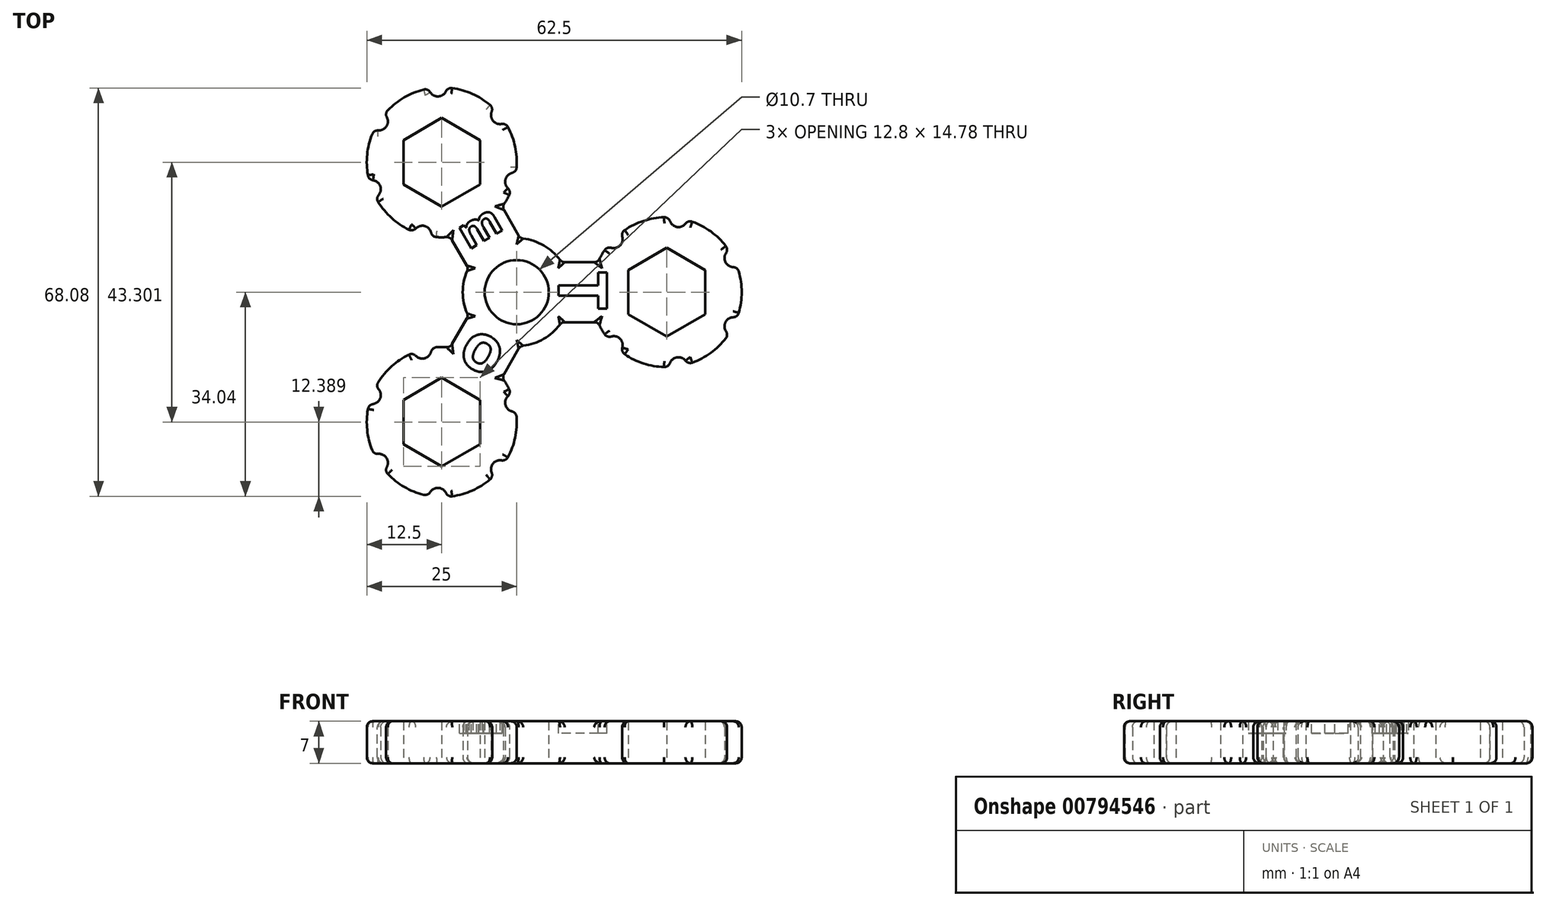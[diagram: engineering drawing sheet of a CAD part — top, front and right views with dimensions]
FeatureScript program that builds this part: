
annotation { "Feature Type Name" : "Feature", "Feature Type Description" : "" }
export const myFeature = defineFeature(function(context is Context, id is Id, definition is map)
    precondition{}
    {
        {
            var Q0;
            Q0=qCreatedBy(makeId("Top.planeOp"),FACE);
            var sketch = newSketch(context, id + "F0", { "sketchPlane" : qUnion([Q0])});
            skCircle(sketch, "E0", {"center": v(0, 0) * mm, "radius": 5.35 * mm});
            skCircle(sketch, "E1", {"center": v(0, 0) * mm, "radius": 9 * mm});
            skCircle(sketch, "E2", {"center": v(25, 0) * mm, "radius": 12.5 * mm});
            skLineSegment(sketch, "E3", {"start": v(7.48, 5) * mm, "end": v(19.48, 5) * mm});
            skLineSegment(sketch, "E4", {"start": v(7.48, -5) * mm, "end": v(19.48, -5) * mm});
            skCircle(sketch, "E5.cCircle", {"center": v(25, 0) * mm, "radius": 6.4 * mm, "construction": true});
            skLineSegment(sketch, "E5.0", {"start": v(31.4, 3.7) * mm, "end": v(31.4, -3.7) * mm});
            skLineSegment(sketch, "E5.1", {"start": v(31.4, -3.7) * mm, "end": v(25, -7.4) * mm});
            skLineSegment(sketch, "E5.2", {"start": v(25, -7.4) * mm, "end": v(18.6, -3.7) * mm});
            skLineSegment(sketch, "E5.3", {"start": v(18.6, -3.7) * mm, "end": v(18.6, 3.7) * mm});
            skLineSegment(sketch, "E5.4", {"start": v(18.6, 3.7) * mm, "end": v(25, 7.4) * mm});
            skLineSegment(sketch, "E5.5", {"start": v(25, 7.4) * mm, "end": v(31.4, 3.7) * mm});
            skPoint(sketch, "E5.0.midPoint", {"position": v(31.4, 0) * mm});
            skCircle(sketch, "E6.1.0", {"center": v(-12.5, 21.65) * mm, "radius": 12.5 * mm});
            skLineSegment(sketch, "E6.1.1", {"start": v(-18.9, 25.35) * mm, "end": v(-12.5, 29.04) * mm});
            skLineSegment(sketch, "E6.1.2", {"start": v(-18.9, 17.96) * mm, "end": v(-18.9, 25.35) * mm});
            skLineSegment(sketch, "E6.1.3", {"start": v(-12.5, 14.26) * mm, "end": v(-18.9, 17.96) * mm});
            skLineSegment(sketch, "E6.1.4", {"start": v(-6.1, 17.96) * mm, "end": v(-12.5, 14.26) * mm});
            skLineSegment(sketch, "E6.1.5", {"start": v(-6.1, 25.35) * mm, "end": v(-6.1, 17.96) * mm});
            skLineSegment(sketch, "E6.1.6", {"start": v(-12.5, 29.04) * mm, "end": v(-6.1, 25.35) * mm});
            skLineSegment(sketch, "E6.1.7", {"start": v(0.59, 8.98) * mm, "end": v(-5.41, 19.37) * mm});
            skLineSegment(sketch, "E6.1.8", {"start": v(-8.07, 3.98) * mm, "end": v(-14.07, 14.37) * mm});
            skCircle(sketch, "E6.2.0", {"center": v(-12.5, -21.65) * mm, "radius": 12.5 * mm});
            skLineSegment(sketch, "E6.2.1", {"start": v(-12.5, -29.04) * mm, "end": v(-18.9, -25.35) * mm});
            skLineSegment(sketch, "E6.2.2", {"start": v(-6.1, -25.35) * mm, "end": v(-12.5, -29.04) * mm});
            skLineSegment(sketch, "E6.2.3", {"start": v(-6.1, -17.96) * mm, "end": v(-6.1, -25.35) * mm});
            skLineSegment(sketch, "E6.2.4", {"start": v(-12.5, -14.26) * mm, "end": v(-6.1, -17.96) * mm});
            skLineSegment(sketch, "E6.2.5", {"start": v(-18.9, -17.96) * mm, "end": v(-12.5, -14.26) * mm});
            skLineSegment(sketch, "E6.2.6", {"start": v(-18.9, -25.35) * mm, "end": v(-18.9, -17.96) * mm});
            skLineSegment(sketch, "E6.2.7", {"start": v(-8.07, -3.98) * mm, "end": v(-14.07, -14.37) * mm});
            skLineSegment(sketch, "E6.2.8", {"start": v(0.59, -8.98) * mm, "end": v(-5.41, -19.37) * mm});
            skLineSegment(sketch, "E7", {"start": v(25, 0) * mm, "end": v(16.16, 8.84) * mm, "construction": true});
            skArc(sketch, "E8", {"start": v(15.17, 7.72) * mm, "mid": v(17.22, 7.78) * mm, "end": v(17.28, 9.83) * mm});
            skArc(sketch, "E9.1.0", {"start": v(25.46, 12.5) * mm, "mid": v(26.72, 10.86) * mm, "end": v(28.42, 12.02) * mm});
            skArc(sketch, "E9.2.0", {"start": v(35.38, 6.97) * mm, "mid": v(34.8, 5) * mm, "end": v(36.74, 4.3) * mm});
            skArc(sketch, "E9.3.0", {"start": v(36.74, -4.3) * mm, "mid": v(34.8, -5) * mm, "end": v(35.38, -6.97) * mm});
            skArc(sketch, "E9.4.0", {"start": v(28.42, -12.02) * mm, "mid": v(26.72, -10.86) * mm, "end": v(25.46, -12.5) * mm});
            skArc(sketch, "E9.5.0", {"start": v(17.28, -9.83) * mm, "mid": v(17.22, -7.78) * mm, "end": v(15.17, -7.72) * mm});
            skLineSegment(sketch, "E9.anchor1", {"start": v(25, 0) * mm, "end": v(15.17, 7.72) * mm, "construction": true});
            skLineSegment(sketch, "E9.anchor2", {"start": v(25, 0) * mm, "end": v(17.28, -9.83) * mm, "construction": true});
            skArc(sketch, "E10.1.0", {"start": v(-14.27, 9.28) * mm, "mid": v(-15.35, 11.03) * mm, "end": v(-17.16, 10.05) * mm});
            skArc(sketch, "E10.1.1", {"start": v(-23.55, 15.8) * mm, "mid": v(-22.77, 17.7) * mm, "end": v(-24.62, 18.6) * mm});
            skArc(sketch, "E10.1.2", {"start": v(-23.72, 27.15) * mm, "mid": v(-21.73, 27.64) * mm, "end": v(-22.1, 29.67) * mm});
            skArc(sketch, "E10.1.3", {"start": v(-14.64, 33.97) * mm, "mid": v(-13.08, 32.64) * mm, "end": v(-11.65, 34.12) * mm});
            skArc(sketch, "E10.1.4", {"start": v(-3.8, 30.62) * mm, "mid": v(-3.95, 28.57) * mm, "end": v(-1.91, 28.3) * mm});
            skArc(sketch, "E10.1.5", {"start": v(-0.13, 19.88) * mm, "mid": v(-1.87, 18.8) * mm, "end": v(-0.9, 17) * mm});
            skArc(sketch, "E10.2.0", {"start": v(-0.9, -17) * mm, "mid": v(-1.87, -18.8) * mm, "end": v(-0.13, -19.88) * mm});
            skArc(sketch, "E10.2.1", {"start": v(-1.91, -28.3) * mm, "mid": v(-3.95, -28.57) * mm, "end": v(-3.8, -30.62) * mm});
            skArc(sketch, "E10.2.2", {"start": v(-11.65, -34.12) * mm, "mid": v(-13.08, -32.64) * mm, "end": v(-14.64, -33.97) * mm});
            skArc(sketch, "E10.2.3", {"start": v(-22.1, -29.67) * mm, "mid": v(-21.73, -27.64) * mm, "end": v(-23.72, -27.15) * mm});
            skArc(sketch, "E10.2.4", {"start": v(-24.62, -18.6) * mm, "mid": v(-22.77, -17.7) * mm, "end": v(-23.55, -15.8) * mm});
            skArc(sketch, "E10.2.5", {"start": v(-17.16, -10.05) * mm, "mid": v(-15.35, -11.03) * mm, "end": v(-14.27, -9.28) * mm});
            skSolve(sketch);
        }
        {
            var Q0;
            Q0=makeQuery(id+"F0.imprint","IMPRINT",FACE,{"disambiguationData":[TD([[makeQuery(id+"F0.imprint","IMPRINT",EDGE,{"derivedFrom":sQuery(id+"F0.wireOp",EDGE,"f4c4e86e-e31c-4c34-a3cf-03a380b0a236.2.0")}),1.0]])]});
            var Q1;
            Q1=makeQuery(id+"F0.imprint","IMPRINT",FACE,{"disambiguationData":[TD([[makeQuery(id+"F0.imprint","IMPRINT",EDGE,{"derivedFrom":sQuery(id+"F0.wireOp",EDGE,"E0")}),-1.0]])]});
            var Q2;
            {var subQ0=sQuery(id+"F0.wireOp",EDGE,"9d0a4749-fec1-4312-9c7e-39d0da4e9910.1.2");var subQ1=sQuery(id+"F0.wireOp",EDGE,"9d0a4749-fec1-4312-9c7e-39d0da4e9910.1.1");var subQ2=makeQuery(id+"F0.imprint","INTERSECT",VERTEX,{"derivedFrom":[subQ1,subQ0]});Q2=makeQuery(id+"F0.imprint","IMPRINT",FACE,{"disambiguationData":[TD([[makeQuery(id+"F0.imprint","IMPRINT",EDGE,{"disambiguationData":[TD([[subQ2,-1.0]])],"derivedFrom":subQ1}),1.0]])]});}
            var Q3;
            {var subQ0=sQuery(id+"F0.wireOp",EDGE,"9d0a4749-fec1-4312-9c7e-39d0da4e9910.2.2");var subQ1=sQuery(id+"F0.wireOp",EDGE,"9d0a4749-fec1-4312-9c7e-39d0da4e9910.2.1");var subQ2=makeQuery(id+"F0.imprint","INTERSECT",VERTEX,{"derivedFrom":[subQ1,subQ0]});Q3=makeQuery(id+"F0.imprint","IMPRINT",FACE,{"disambiguationData":[TD([[makeQuery(id+"F0.imprint","IMPRINT",EDGE,{"disambiguationData":[TD([[subQ2,-1.0]])],"derivedFrom":subQ1}),1.0]])]});}
            var Q4;
            Q4=makeQuery(id+"F0.imprint","IMPRINT",FACE,{"disambiguationData":[TD([[makeQuery(id+"F0.imprint","IMPRINT",EDGE,{"derivedFrom":sQuery(id+"F0.wireOp",EDGE,"f4c4e86e-e31c-4c34-a3cf-03a380b0a236.1.0")}),1.0]])]});
            var Q5;
            {var subQ0=sQuery(id+"F0.wireOp",EDGE,"E3");var subQ1=sQuery(id+"F0.wireOp",EDGE,"E1");var subQ2=makeQuery(id+"F0.imprint","INTERSECT",VERTEX,{"derivedFrom":[subQ1,subQ0]});Q5=makeQuery(id+"F0.imprint","IMPRINT",FACE,{"disambiguationData":[TD([[makeQuery(id+"F0.imprint","IMPRINT",EDGE,{"disambiguationData":[TD([[subQ2,1.0]])],"derivedFrom":subQ1}),-1.0]])]});}
            var Q6;
            {var subQ0=sQuery(id+"F0.wireOp",EDGE,"E4");var subQ1=sQuery(id+"F0.wireOp",EDGE,"d638fde7-8053-48f4-9a89-c2a8404b4ae3.3");var subQ2=makeQuery(id+"F0.imprint","INTERSECT",VERTEX,{"derivedFrom":[subQ1,subQ0]});Q6=makeQuery(id+"F0.imprint","IMPRINT",FACE,{"disambiguationData":[TD([[makeQuery(id+"F0.imprint","IMPRINT",EDGE,{"disambiguationData":[TD([[subQ2,-1.0]])],"derivedFrom":subQ1}),1.0]])]});}
            var Q7;
            {var subQ0=sQuery(id+"F0.wireOp",EDGE,"9d0a4749-fec1-4312-9c7e-39d0da4e9910.1.2");var subQ1=sQuery(id+"F0.wireOp",EDGE,"E1");var subQ2=makeQuery(id+"F0.imprint","INTERSECT",VERTEX,{"derivedFrom":[subQ1,subQ0]});Q7=makeQuery(id+"F0.imprint","IMPRINT",FACE,{"disambiguationData":[TD([[makeQuery(id+"F0.imprint","IMPRINT",EDGE,{"disambiguationData":[TD([[subQ2,1.0]])],"derivedFrom":subQ1}),-1.0]])]});}
            var Q8;
            {var subQ0=sQuery(id+"F0.wireOp",EDGE,"9d0a4749-fec1-4312-9c7e-39d0da4e9910.2.2");var subQ1=sQuery(id+"F0.wireOp",EDGE,"E1");var subQ2=makeQuery(id+"F0.imprint","INTERSECT",VERTEX,{"derivedFrom":[subQ1,subQ0]});Q8=makeQuery(id+"F0.imprint","IMPRINT",FACE,{"disambiguationData":[TD([[makeQuery(id+"F0.imprint","IMPRINT",EDGE,{"disambiguationData":[TD([[subQ2,1.0]])],"derivedFrom":subQ1}),-1.0]])]});}
            var Q9;
            Q9=makeQuery(id+"F0.imprint","IMPRINT",FACE,{"disambiguationData":[TD([[makeQuery(id+"F0.imprint","IMPRINT",EDGE,{"derivedFrom":sQuery(id+"F0.wireOp",EDGE,"d638fde7-8053-48f4-9a89-c2a8404b4ae3.0")}),1.0]])]});
            var Q10;
            {var subQ0=sQuery(id+"F0.wireOp",EDGE,"E3");var subQ1=sQuery(id+"F0.wireOp",EDGE,"E2");var subQ2=makeQuery(id+"F0.imprint","INTERSECT",VERTEX,{"derivedFrom":[subQ1,subQ0]});Q10=makeQuery(id+"F0.imprint","IMPRINT",FACE,{"disambiguationData":[TD([[makeQuery(id+"F0.imprint","IMPRINT",EDGE,{"disambiguationData":[TD([[subQ2,-1.0]])],"derivedFrom":subQ1}),1.0]])]});}
            var Q11;
            {var subQ0=sQuery(id+"F0.wireOp",EDGE,"E3");var subQ1=sQuery(id+"F0.wireOp",EDGE,"E2");var subQ2=makeQuery(id+"F0.imprint","INTERSECT",VERTEX,{"derivedFrom":[subQ1,subQ0]});Q11=makeQuery(id+"F0.imprint","IMPRINT",FACE,{"disambiguationData":[TD([[makeQuery(id+"F0.imprint","IMPRINT",EDGE,{"disambiguationData":[TD([[subQ2,1.0]])],"derivedFrom":subQ1}),1.0]])]});}
            var Q12;
            {var subQ0=sQuery(id+"F0.wireOp",EDGE,"9d0a4749-fec1-4312-9c7e-39d0da4e9910.2.2");var subQ1=sQuery(id+"F0.wireOp",EDGE,"9d0a4749-fec1-4312-9c7e-39d0da4e9910.2.1");var subQ2=makeQuery(id+"F0.imprint","INTERSECT",VERTEX,{"derivedFrom":[subQ1,subQ0]});Q12=makeQuery(id+"F0.imprint","IMPRINT",FACE,{"disambiguationData":[TD([[makeQuery(id+"F0.imprint","IMPRINT",EDGE,{"disambiguationData":[TD([[subQ2,1.0]])],"derivedFrom":subQ1}),1.0]])]});}
            var Q13;
            {var subQ0=sQuery(id+"F0.wireOp",EDGE,"9d0a4749-fec1-4312-9c7e-39d0da4e9910.1.2");var subQ1=sQuery(id+"F0.wireOp",EDGE,"9d0a4749-fec1-4312-9c7e-39d0da4e9910.1.1");var subQ2=makeQuery(id+"F0.imprint","INTERSECT",VERTEX,{"derivedFrom":[subQ1,subQ0]});Q13=makeQuery(id+"F0.imprint","IMPRINT",FACE,{"disambiguationData":[TD([[makeQuery(id+"F0.imprint","IMPRINT",EDGE,{"disambiguationData":[TD([[subQ2,1.0]])],"derivedFrom":subQ1}),1.0]])]});}
            var Q14;
            Q14=makeQuery(id+"F0.imprint","IMPRINT",FACE,{"disambiguationData":[TD([[makeQuery(id+"F0.imprint","IMPRINT",EDGE,{"derivedFrom":sQuery(id+"F0.wireOp",EDGE,"E6.1.1")}),1.0]])]});
            var Q15;
            Q15=makeQuery(id+"F0.imprint","IMPRINT",FACE,{"disambiguationData":[TD([[makeQuery(id+"F0.imprint","IMPRINT",EDGE,{"derivedFrom":sQuery(id+"F0.wireOp",EDGE,"E6.2.1")}),1.0]])]});
            extrude(context, id + "F1", {"entities" : qUnion([Q0, Q1, Q2, Q3, Q4, Q5, Q6, Q7, Q8, Q9, Q10, Q11, Q12, Q13, Q14, Q15]), "depth" : 7 * mm, "offsetDistance" : 25 * mm});
        }
        {
            var Q0;
            {var subQ0=sQuery(id+"F0.wireOp",EDGE,"E6.1.0");Q0=makeQuery(id+"F1.opExtrude","CAP_EDGE",EDGE,{"disambiguationData":[OSD([subQ0]),TDD([makeQuery(id+"F0.imprint","IMPRINT",EDGE,{"disambiguationData":[TD([[makeQuery(id+"F0.imprint","INTERSECT",VERTEX,{"disambiguationData":[OD(1.0)],"derivedFrom":[subQ0,sQuery(id+"F0.wireOp",EDGE,"E10.1.0")]}),1.0]])],"derivedFrom":subQ0})])],"isStart":true});}
            var Q1;
            {var subQ0=sQuery(id+"F0.wireOp",EDGE,"E6.1.0");Q1=makeQuery(id+"F1.opExtrude","CAP_EDGE",EDGE,{"disambiguationData":[OSD([subQ0]),TDD([makeQuery(id+"F0.imprint","IMPRINT",EDGE,{"disambiguationData":[TD([[makeQuery(id+"F0.imprint","INTERSECT",VERTEX,{"disambiguationData":[OD(0.0)],"derivedFrom":[subQ0,sQuery(id+"F0.wireOp",EDGE,"E10.1.0")]}),-1.0]])],"derivedFrom":subQ0})])],"isStart":true});}
            var Q2;
            {var subQ0=sQuery(id+"F0.wireOp",EDGE,"E6.1.0");Q2=makeQuery(id+"F1.opExtrude","CAP_EDGE",EDGE,{"disambiguationData":[OSD([subQ0]),TDD([makeQuery(id+"F0.imprint","IMPRINT",EDGE,{"disambiguationData":[TD([[makeQuery(id+"F0.imprint","INTERSECT",VERTEX,{"disambiguationData":[OD(1.0)],"derivedFrom":[subQ0,sQuery(id+"F0.wireOp",EDGE,"E10.1.5")]}),1.0]])],"derivedFrom":subQ0})])],"isStart":true});}
            var Q3;
            {var subQ0=sQuery(id+"F0.wireOp",EDGE,"E6.1.0");Q3=makeQuery(id+"F1.opExtrude","CAP_EDGE",EDGE,{"disambiguationData":[OSD([subQ0]),TDD([makeQuery(id+"F0.imprint","IMPRINT",EDGE,{"disambiguationData":[TD([[makeQuery(id+"F0.imprint","INTERSECT",VERTEX,{"disambiguationData":[OD(1.0)],"derivedFrom":[subQ0,sQuery(id+"F0.wireOp",EDGE,"E10.1.4")]}),1.0]])],"derivedFrom":subQ0})])],"isStart":true});}
            var Q4;
            {var subQ0=sQuery(id+"F0.wireOp",EDGE,"E6.1.0");Q4=makeQuery(id+"F1.opExtrude","CAP_EDGE",EDGE,{"disambiguationData":[OSD([subQ0]),TDD([makeQuery(id+"F0.imprint","IMPRINT",EDGE,{"disambiguationData":[TD([[makeQuery(id+"F0.imprint","INTERSECT",VERTEX,{"disambiguationData":[OD(1.0)],"derivedFrom":[subQ0,sQuery(id+"F0.wireOp",EDGE,"E10.1.3")]}),1.0]])],"derivedFrom":subQ0})])],"isStart":true});}
            var Q5;
            {var subQ0=sQuery(id+"F0.wireOp",EDGE,"E6.1.0");Q5=makeQuery(id+"F1.opExtrude","CAP_EDGE",EDGE,{"disambiguationData":[OSD([subQ0]),TDD([makeQuery(id+"F0.imprint","IMPRINT",EDGE,{"disambiguationData":[TD([[makeQuery(id+"F0.imprint","INTERSECT",VERTEX,{"disambiguationData":[OD(1.0)],"derivedFrom":[subQ0,sQuery(id+"F0.wireOp",EDGE,"E10.1.2")]}),1.0]])],"derivedFrom":subQ0})])],"isStart":true});}
            var Q6;
            Q6=makeQuery(id+"F1.opExtrude","CAP_EDGE",EDGE,{"disambiguationData":[OSD([sQuery(id+"F0.wireOp",EDGE,"E6.1.8")])],"isStart":false});
            var Q7;
            {var subQ0=sQuery(id+"F0.wireOp",EDGE,"E1");Q7=makeQuery(id+"F1.opExtrude","CAP_EDGE",EDGE,{"disambiguationData":[OSD([subQ0]),TDD([makeQuery(id+"F0.imprint","IMPRINT",EDGE,{"disambiguationData":[TD([[makeQuery(id+"F0.imprint","INTERSECT",VERTEX,{"derivedFrom":[subQ0,sQuery(id+"F0.wireOp",EDGE,"E6.1.8")]}),-1.0]])],"derivedFrom":subQ0})])],"isStart":false});}
            var Q8;
            Q8=makeQuery(id+"F1.opExtrude","CAP_EDGE",EDGE,{"disambiguationData":[OSD([sQuery(id+"F0.wireOp",EDGE,"E6.2.7")])],"isStart":false});
            var Q9;
            {var subQ0=sQuery(id+"F0.wireOp",EDGE,"E6.2.0");Q9=makeQuery(id+"F1.opExtrude","CAP_EDGE",EDGE,{"disambiguationData":[OSD([subQ0]),TDD([makeQuery(id+"F0.imprint","IMPRINT",EDGE,{"disambiguationData":[TD([[makeQuery(id+"F0.imprint","INTERSECT",VERTEX,{"disambiguationData":[OD(1.0)],"derivedFrom":[subQ0,sQuery(id+"F0.wireOp",EDGE,"E10.2.1")]}),1.0]])],"derivedFrom":subQ0})])],"isStart":false});}
            var Q10;
            {var subQ0=sQuery(id+"F0.wireOp",EDGE,"E6.2.0");Q10=makeQuery(id+"F1.opExtrude","CAP_EDGE",EDGE,{"disambiguationData":[OSD([subQ0]),TDD([makeQuery(id+"F0.imprint","IMPRINT",EDGE,{"disambiguationData":[TD([[makeQuery(id+"F0.imprint","INTERSECT",VERTEX,{"disambiguationData":[OD(1.0)],"derivedFrom":[subQ0,sQuery(id+"F0.wireOp",EDGE,"E10.2.0")]}),1.0]])],"derivedFrom":subQ0})])],"isStart":false});}
            var Q11;
            {var subQ0=sQuery(id+"F0.wireOp",EDGE,"E6.2.0");Q11=makeQuery(id+"F1.opExtrude","CAP_EDGE",EDGE,{"disambiguationData":[OSD([subQ0]),TDD([makeQuery(id+"F0.imprint","IMPRINT",EDGE,{"disambiguationData":[TD([[makeQuery(id+"F0.imprint","INTERSECT",VERTEX,{"disambiguationData":[OD(0.0)],"derivedFrom":[subQ0,sQuery(id+"F0.wireOp",EDGE,"E10.2.0")]}),-1.0]])],"derivedFrom":subQ0})])],"isStart":false});}
            var Q12;
            {var subQ0=sQuery(id+"F0.wireOp",EDGE,"E6.2.0");Q12=makeQuery(id+"F1.opExtrude","CAP_EDGE",EDGE,{"disambiguationData":[OSD([subQ0]),TDD([makeQuery(id+"F0.imprint","IMPRINT",EDGE,{"disambiguationData":[TD([[makeQuery(id+"F0.imprint","INTERSECT",VERTEX,{"disambiguationData":[OD(1.0)],"derivedFrom":[subQ0,sQuery(id+"F0.wireOp",EDGE,"E10.2.5")]}),1.0]])],"derivedFrom":subQ0})])],"isStart":false});}
            var Q13;
            {var subQ0=sQuery(id+"F0.wireOp",EDGE,"E6.2.0");Q13=makeQuery(id+"F1.opExtrude","CAP_EDGE",EDGE,{"disambiguationData":[OSD([subQ0]),TDD([makeQuery(id+"F0.imprint","IMPRINT",EDGE,{"disambiguationData":[TD([[makeQuery(id+"F0.imprint","INTERSECT",VERTEX,{"disambiguationData":[OD(1.0)],"derivedFrom":[subQ0,sQuery(id+"F0.wireOp",EDGE,"E10.2.4")]}),1.0]])],"derivedFrom":subQ0})])],"isStart":false});}
            var Q14;
            {var subQ0=sQuery(id+"F0.wireOp",EDGE,"E6.2.0");Q14=makeQuery(id+"F1.opExtrude","CAP_EDGE",EDGE,{"disambiguationData":[OSD([subQ0]),TDD([makeQuery(id+"F0.imprint","IMPRINT",EDGE,{"disambiguationData":[TD([[makeQuery(id+"F0.imprint","INTERSECT",VERTEX,{"disambiguationData":[OD(1.0)],"derivedFrom":[subQ0,sQuery(id+"F0.wireOp",EDGE,"E10.2.3")]}),1.0]])],"derivedFrom":subQ0})])],"isStart":false});}
            var Q15;
            {var subQ0=sQuery(id+"F0.wireOp",EDGE,"E6.2.0");Q15=makeQuery(id+"F1.opExtrude","CAP_EDGE",EDGE,{"disambiguationData":[OSD([subQ0]),TDD([makeQuery(id+"F0.imprint","IMPRINT",EDGE,{"disambiguationData":[TD([[makeQuery(id+"F0.imprint","INTERSECT",VERTEX,{"disambiguationData":[OD(1.0)],"derivedFrom":[subQ0,sQuery(id+"F0.wireOp",EDGE,"E10.2.2")]}),1.0]])],"derivedFrom":subQ0})])],"isStart":false});}
            var Q16;
            Q16=makeQuery(id+"F1.opExtrude","CAP_EDGE",EDGE,{"disambiguationData":[OSD([sQuery(id+"F0.wireOp",EDGE,"E6.2.8")])],"isStart":false});
            var Q17;
            {var subQ0=sQuery(id+"F0.wireOp",EDGE,"E1");Q17=makeQuery(id+"F1.opExtrude","CAP_EDGE",EDGE,{"disambiguationData":[OSD([subQ0]),TDD([makeQuery(id+"F0.imprint","IMPRINT",EDGE,{"disambiguationData":[TD([[makeQuery(id+"F0.imprint","INTERSECT",VERTEX,{"derivedFrom":[subQ0,sQuery(id+"F0.wireOp",EDGE,"E4")]}),1.0]])],"derivedFrom":subQ0})])],"isStart":false});}
            var Q18;
            Q18=makeQuery(id+"F1.opExtrude","CAP_EDGE",EDGE,{"disambiguationData":[OSD([sQuery(id+"F0.wireOp",EDGE,"E4")])],"isStart":false});
            var Q19;
            {var subQ0=sQuery(id+"F0.wireOp",EDGE,"E2");Q19=makeQuery(id+"F1.opExtrude","CAP_EDGE",EDGE,{"disambiguationData":[OSD([subQ0]),TDD([makeQuery(id+"F0.imprint","IMPRINT",EDGE,{"disambiguationData":[TD([[makeQuery(id+"F0.imprint","INTERSECT",VERTEX,{"disambiguationData":[OD(1.0)],"derivedFrom":[subQ0,sQuery(id+"F0.wireOp",EDGE,"E9.1.0")]}),1.0]])],"derivedFrom":subQ0})])],"isStart":false});}
            var Q20;
            {var subQ0=sQuery(id+"F0.wireOp",EDGE,"E2");Q20=makeQuery(id+"F1.opExtrude","CAP_EDGE",EDGE,{"disambiguationData":[OSD([subQ0]),TDD([makeQuery(id+"F0.imprint","IMPRINT",EDGE,{"disambiguationData":[TD([[makeQuery(id+"F0.imprint","INTERSECT",VERTEX,{"disambiguationData":[OD(1.0)],"derivedFrom":[subQ0,sQuery(id+"F0.wireOp",EDGE,"E8")]}),1.0]])],"derivedFrom":subQ0})])],"isStart":false});}
            var Q21;
            {var subQ0=sQuery(id+"F0.wireOp",EDGE,"E2");Q21=makeQuery(id+"F1.opExtrude","CAP_EDGE",EDGE,{"disambiguationData":[OSD([subQ0]),TDD([makeQuery(id+"F0.imprint","IMPRINT",EDGE,{"disambiguationData":[TD([[makeQuery(id+"F0.imprint","INTERSECT",VERTEX,{"disambiguationData":[OD(0.0)],"derivedFrom":[subQ0,sQuery(id+"F0.wireOp",EDGE,"E8")]}),-1.0]])],"derivedFrom":subQ0})])],"isStart":false});}
            var Q22;
            {var subQ0=sQuery(id+"F0.wireOp",EDGE,"E2");Q22=makeQuery(id+"F1.opExtrude","CAP_EDGE",EDGE,{"disambiguationData":[OSD([subQ0]),TDD([makeQuery(id+"F0.imprint","IMPRINT",EDGE,{"disambiguationData":[TD([[makeQuery(id+"F0.imprint","INTERSECT",VERTEX,{"disambiguationData":[OD(1.0)],"derivedFrom":[subQ0,sQuery(id+"F0.wireOp",EDGE,"E9.5.0")]}),1.0]])],"derivedFrom":subQ0})])],"isStart":false});}
            var Q23;
            {var subQ0=sQuery(id+"F0.wireOp",EDGE,"E2");Q23=makeQuery(id+"F1.opExtrude","CAP_EDGE",EDGE,{"disambiguationData":[OSD([subQ0]),TDD([makeQuery(id+"F0.imprint","IMPRINT",EDGE,{"disambiguationData":[TD([[makeQuery(id+"F0.imprint","INTERSECT",VERTEX,{"disambiguationData":[OD(1.0)],"derivedFrom":[subQ0,sQuery(id+"F0.wireOp",EDGE,"E9.4.0")]}),1.0]])],"derivedFrom":subQ0})])],"isStart":false});}
            var Q24;
            {var subQ0=sQuery(id+"F0.wireOp",EDGE,"E2");Q24=makeQuery(id+"F1.opExtrude","CAP_EDGE",EDGE,{"disambiguationData":[OSD([subQ0]),TDD([makeQuery(id+"F0.imprint","IMPRINT",EDGE,{"disambiguationData":[TD([[makeQuery(id+"F0.imprint","INTERSECT",VERTEX,{"disambiguationData":[OD(1.0)],"derivedFrom":[subQ0,sQuery(id+"F0.wireOp",EDGE,"E9.3.0")]}),1.0]])],"derivedFrom":subQ0})])],"isStart":false});}
            var Q25;
            {var subQ0=sQuery(id+"F0.wireOp",EDGE,"E2");Q25=makeQuery(id+"F1.opExtrude","CAP_EDGE",EDGE,{"disambiguationData":[OSD([subQ0]),TDD([makeQuery(id+"F0.imprint","IMPRINT",EDGE,{"disambiguationData":[TD([[makeQuery(id+"F0.imprint","INTERSECT",VERTEX,{"disambiguationData":[OD(1.0)],"derivedFrom":[subQ0,sQuery(id+"F0.wireOp",EDGE,"E9.2.0")]}),1.0]])],"derivedFrom":subQ0})])],"isStart":false});}
            var Q26;
            Q26=makeQuery(id+"F1.opExtrude","CAP_EDGE",EDGE,{"disambiguationData":[OSD([sQuery(id+"F0.wireOp",EDGE,"E3")])],"isStart":false});
            var Q27;
            {var subQ0=sQuery(id+"F0.wireOp",EDGE,"E1");Q27=makeQuery(id+"F1.opExtrude","CAP_EDGE",EDGE,{"disambiguationData":[OSD([subQ0]),TDD([makeQuery(id+"F0.imprint","IMPRINT",EDGE,{"disambiguationData":[TD([[makeQuery(id+"F0.imprint","INTERSECT",VERTEX,{"derivedFrom":[subQ0,sQuery(id+"F0.wireOp",EDGE,"E3")]}),-1.0]])],"derivedFrom":subQ0})])],"isStart":false});}
            var Q28;
            Q28=makeQuery(id+"F1.opExtrude","CAP_EDGE",EDGE,{"disambiguationData":[OSD([sQuery(id+"F0.wireOp",EDGE,"E6.1.7")])],"isStart":false});
            var Q29;
            {var subQ0=sQuery(id+"F0.wireOp",EDGE,"E6.1.0");Q29=makeQuery(id+"F1.opExtrude","CAP_EDGE",EDGE,{"disambiguationData":[OSD([subQ0]),TDD([makeQuery(id+"F0.imprint","IMPRINT",EDGE,{"disambiguationData":[TD([[makeQuery(id+"F0.imprint","INTERSECT",VERTEX,{"disambiguationData":[OD(1.0)],"derivedFrom":[subQ0,sQuery(id+"F0.wireOp",EDGE,"E10.1.1")]}),1.0]])],"derivedFrom":subQ0})])],"isStart":false});}
            var Q30;
            {var subQ0=sQuery(id+"F0.wireOp",EDGE,"E6.1.0");Q30=makeQuery(id+"F1.opExtrude","CAP_EDGE",EDGE,{"disambiguationData":[OSD([subQ0]),TDD([makeQuery(id+"F0.imprint","IMPRINT",EDGE,{"disambiguationData":[TD([[makeQuery(id+"F0.imprint","INTERSECT",VERTEX,{"disambiguationData":[OD(1.0)],"derivedFrom":[subQ0,sQuery(id+"F0.wireOp",EDGE,"E10.1.0")]}),1.0]])],"derivedFrom":subQ0})])],"isStart":false});}
            var Q31;
            {var subQ0=sQuery(id+"F0.wireOp",EDGE,"E6.1.0");Q31=makeQuery(id+"F1.opExtrude","CAP_EDGE",EDGE,{"disambiguationData":[OSD([subQ0]),TDD([makeQuery(id+"F0.imprint","IMPRINT",EDGE,{"disambiguationData":[TD([[makeQuery(id+"F0.imprint","INTERSECT",VERTEX,{"disambiguationData":[OD(0.0)],"derivedFrom":[subQ0,sQuery(id+"F0.wireOp",EDGE,"E10.1.0")]}),-1.0]])],"derivedFrom":subQ0})])],"isStart":false});}
            var Q32;
            {var subQ0=sQuery(id+"F0.wireOp",EDGE,"E6.1.0");Q32=makeQuery(id+"F1.opExtrude","CAP_EDGE",EDGE,{"disambiguationData":[OSD([subQ0]),TDD([makeQuery(id+"F0.imprint","IMPRINT",EDGE,{"disambiguationData":[TD([[makeQuery(id+"F0.imprint","INTERSECT",VERTEX,{"disambiguationData":[OD(1.0)],"derivedFrom":[subQ0,sQuery(id+"F0.wireOp",EDGE,"E10.1.5")]}),1.0]])],"derivedFrom":subQ0})])],"isStart":false});}
            var Q33;
            {var subQ0=sQuery(id+"F0.wireOp",EDGE,"E6.1.0");Q33=makeQuery(id+"F1.opExtrude","CAP_EDGE",EDGE,{"disambiguationData":[OSD([subQ0]),TDD([makeQuery(id+"F0.imprint","IMPRINT",EDGE,{"disambiguationData":[TD([[makeQuery(id+"F0.imprint","INTERSECT",VERTEX,{"disambiguationData":[OD(1.0)],"derivedFrom":[subQ0,sQuery(id+"F0.wireOp",EDGE,"E10.1.4")]}),1.0]])],"derivedFrom":subQ0})])],"isStart":false});}
            var Q34;
            {var subQ0=sQuery(id+"F0.wireOp",EDGE,"E6.1.0");Q34=makeQuery(id+"F1.opExtrude","CAP_EDGE",EDGE,{"disambiguationData":[OSD([subQ0]),TDD([makeQuery(id+"F0.imprint","IMPRINT",EDGE,{"disambiguationData":[TD([[makeQuery(id+"F0.imprint","INTERSECT",VERTEX,{"disambiguationData":[OD(1.0)],"derivedFrom":[subQ0,sQuery(id+"F0.wireOp",EDGE,"E10.1.3")]}),1.0]])],"derivedFrom":subQ0})])],"isStart":false});}
            var Q35;
            {var subQ0=sQuery(id+"F0.wireOp",EDGE,"E6.1.0");Q35=makeQuery(id+"F1.opExtrude","CAP_EDGE",EDGE,{"disambiguationData":[OSD([subQ0]),TDD([makeQuery(id+"F0.imprint","IMPRINT",EDGE,{"disambiguationData":[TD([[makeQuery(id+"F0.imprint","INTERSECT",VERTEX,{"disambiguationData":[OD(1.0)],"derivedFrom":[subQ0,sQuery(id+"F0.wireOp",EDGE,"E10.1.2")]}),1.0]])],"derivedFrom":subQ0})])],"isStart":false});}
            var Q36;
            {var subQ0=sQuery(id+"F0.wireOp",EDGE,"E1");Q36=makeQuery(id+"F1.opExtrude","CAP_EDGE",EDGE,{"disambiguationData":[OSD([subQ0]),TDD([makeQuery(id+"F0.imprint","IMPRINT",EDGE,{"disambiguationData":[TD([[makeQuery(id+"F0.imprint","INTERSECT",VERTEX,{"derivedFrom":[subQ0,sQuery(id+"F0.wireOp",EDGE,"E6.1.8")]}),-1.0]])],"derivedFrom":subQ0})])],"isStart":true});}
            var Q37;
            {var subQ0=sQuery(id+"F0.wireOp",EDGE,"E6.2.0");Q37=makeQuery(id+"F1.opExtrude","CAP_EDGE",EDGE,{"disambiguationData":[OSD([subQ0]),TDD([makeQuery(id+"F0.imprint","IMPRINT",EDGE,{"disambiguationData":[TD([[makeQuery(id+"F0.imprint","INTERSECT",VERTEX,{"disambiguationData":[OD(1.0)],"derivedFrom":[subQ0,sQuery(id+"F0.wireOp",EDGE,"E10.2.1")]}),1.0]])],"derivedFrom":subQ0})])],"isStart":true});}
            var Q38;
            {var subQ0=sQuery(id+"F0.wireOp",EDGE,"E6.2.0");Q38=makeQuery(id+"F1.opExtrude","CAP_EDGE",EDGE,{"disambiguationData":[OSD([subQ0]),TDD([makeQuery(id+"F0.imprint","IMPRINT",EDGE,{"disambiguationData":[TD([[makeQuery(id+"F0.imprint","INTERSECT",VERTEX,{"disambiguationData":[OD(1.0)],"derivedFrom":[subQ0,sQuery(id+"F0.wireOp",EDGE,"E10.2.0")]}),1.0]])],"derivedFrom":subQ0})])],"isStart":true});}
            var Q39;
            {var subQ0=sQuery(id+"F0.wireOp",EDGE,"E6.2.0");Q39=makeQuery(id+"F1.opExtrude","CAP_EDGE",EDGE,{"disambiguationData":[OSD([subQ0]),TDD([makeQuery(id+"F0.imprint","IMPRINT",EDGE,{"disambiguationData":[TD([[makeQuery(id+"F0.imprint","INTERSECT",VERTEX,{"disambiguationData":[OD(0.0)],"derivedFrom":[subQ0,sQuery(id+"F0.wireOp",EDGE,"E10.2.0")]}),-1.0]])],"derivedFrom":subQ0})])],"isStart":true});}
            var Q40;
            {var subQ0=sQuery(id+"F0.wireOp",EDGE,"E6.2.0");Q40=makeQuery(id+"F1.opExtrude","CAP_EDGE",EDGE,{"disambiguationData":[OSD([subQ0]),TDD([makeQuery(id+"F0.imprint","IMPRINT",EDGE,{"disambiguationData":[TD([[makeQuery(id+"F0.imprint","INTERSECT",VERTEX,{"disambiguationData":[OD(1.0)],"derivedFrom":[subQ0,sQuery(id+"F0.wireOp",EDGE,"E10.2.5")]}),1.0]])],"derivedFrom":subQ0})])],"isStart":true});}
            var Q41;
            {var subQ0=sQuery(id+"F0.wireOp",EDGE,"E6.2.0");Q41=makeQuery(id+"F1.opExtrude","CAP_EDGE",EDGE,{"disambiguationData":[OSD([subQ0]),TDD([makeQuery(id+"F0.imprint","IMPRINT",EDGE,{"disambiguationData":[TD([[makeQuery(id+"F0.imprint","INTERSECT",VERTEX,{"disambiguationData":[OD(1.0)],"derivedFrom":[subQ0,sQuery(id+"F0.wireOp",EDGE,"E10.2.4")]}),1.0]])],"derivedFrom":subQ0})])],"isStart":true});}
            var Q42;
            {var subQ0=sQuery(id+"F0.wireOp",EDGE,"E6.2.0");Q42=makeQuery(id+"F1.opExtrude","CAP_EDGE",EDGE,{"disambiguationData":[OSD([subQ0]),TDD([makeQuery(id+"F0.imprint","IMPRINT",EDGE,{"disambiguationData":[TD([[makeQuery(id+"F0.imprint","INTERSECT",VERTEX,{"disambiguationData":[OD(1.0)],"derivedFrom":[subQ0,sQuery(id+"F0.wireOp",EDGE,"E10.2.3")]}),1.0]])],"derivedFrom":subQ0})])],"isStart":true});}
            var Q43;
            {var subQ0=sQuery(id+"F0.wireOp",EDGE,"E6.2.0");Q43=makeQuery(id+"F1.opExtrude","CAP_EDGE",EDGE,{"disambiguationData":[OSD([subQ0]),TDD([makeQuery(id+"F0.imprint","IMPRINT",EDGE,{"disambiguationData":[TD([[makeQuery(id+"F0.imprint","INTERSECT",VERTEX,{"disambiguationData":[OD(1.0)],"derivedFrom":[subQ0,sQuery(id+"F0.wireOp",EDGE,"E10.2.2")]}),1.0]])],"derivedFrom":subQ0})])],"isStart":true});}
            var Q44;
            Q44=makeQuery(id+"F1.opExtrude","CAP_EDGE",EDGE,{"disambiguationData":[OSD([sQuery(id+"F0.wireOp",EDGE,"E6.2.8")])],"isStart":true});
            var Q45;
            {var subQ0=sQuery(id+"F0.wireOp",EDGE,"E1");Q45=makeQuery(id+"F1.opExtrude","CAP_EDGE",EDGE,{"disambiguationData":[OSD([subQ0]),TDD([makeQuery(id+"F0.imprint","IMPRINT",EDGE,{"disambiguationData":[TD([[makeQuery(id+"F0.imprint","INTERSECT",VERTEX,{"derivedFrom":[subQ0,sQuery(id+"F0.wireOp",EDGE,"E4")]}),1.0]])],"derivedFrom":subQ0})])],"isStart":true});}
            var Q46;
            Q46=makeQuery(id+"F1.opExtrude","CAP_EDGE",EDGE,{"disambiguationData":[OSD([sQuery(id+"F0.wireOp",EDGE,"E4")])],"isStart":true});
            var Q47;
            {var subQ0=sQuery(id+"F0.wireOp",EDGE,"E2");Q47=makeQuery(id+"F1.opExtrude","CAP_EDGE",EDGE,{"disambiguationData":[OSD([subQ0]),TDD([makeQuery(id+"F0.imprint","IMPRINT",EDGE,{"disambiguationData":[TD([[makeQuery(id+"F0.imprint","INTERSECT",VERTEX,{"disambiguationData":[OD(1.0)],"derivedFrom":[subQ0,sQuery(id+"F0.wireOp",EDGE,"E9.1.0")]}),1.0]])],"derivedFrom":subQ0})])],"isStart":true});}
            var Q48;
            {var subQ0=sQuery(id+"F0.wireOp",EDGE,"E2");Q48=makeQuery(id+"F1.opExtrude","CAP_EDGE",EDGE,{"disambiguationData":[OSD([subQ0]),TDD([makeQuery(id+"F0.imprint","IMPRINT",EDGE,{"disambiguationData":[TD([[makeQuery(id+"F0.imprint","INTERSECT",VERTEX,{"disambiguationData":[OD(1.0)],"derivedFrom":[subQ0,sQuery(id+"F0.wireOp",EDGE,"E8")]}),1.0]])],"derivedFrom":subQ0})])],"isStart":true});}
            var Q49;
            {var subQ0=sQuery(id+"F0.wireOp",EDGE,"E2");Q49=makeQuery(id+"F1.opExtrude","CAP_EDGE",EDGE,{"disambiguationData":[OSD([subQ0]),TDD([makeQuery(id+"F0.imprint","IMPRINT",EDGE,{"disambiguationData":[TD([[makeQuery(id+"F0.imprint","INTERSECT",VERTEX,{"disambiguationData":[OD(0.0)],"derivedFrom":[subQ0,sQuery(id+"F0.wireOp",EDGE,"E8")]}),-1.0]])],"derivedFrom":subQ0})])],"isStart":true});}
            var Q50;
            {var subQ0=sQuery(id+"F0.wireOp",EDGE,"E2");Q50=makeQuery(id+"F1.opExtrude","CAP_EDGE",EDGE,{"disambiguationData":[OSD([subQ0]),TDD([makeQuery(id+"F0.imprint","IMPRINT",EDGE,{"disambiguationData":[TD([[makeQuery(id+"F0.imprint","INTERSECT",VERTEX,{"disambiguationData":[OD(1.0)],"derivedFrom":[subQ0,sQuery(id+"F0.wireOp",EDGE,"E9.5.0")]}),1.0]])],"derivedFrom":subQ0})])],"isStart":true});}
            var Q51;
            {var subQ0=sQuery(id+"F0.wireOp",EDGE,"E2");Q51=makeQuery(id+"F1.opExtrude","CAP_EDGE",EDGE,{"disambiguationData":[OSD([subQ0]),TDD([makeQuery(id+"F0.imprint","IMPRINT",EDGE,{"disambiguationData":[TD([[makeQuery(id+"F0.imprint","INTERSECT",VERTEX,{"disambiguationData":[OD(1.0)],"derivedFrom":[subQ0,sQuery(id+"F0.wireOp",EDGE,"E9.4.0")]}),1.0]])],"derivedFrom":subQ0})])],"isStart":true});}
            var Q52;
            {var subQ0=sQuery(id+"F0.wireOp",EDGE,"E2");Q52=makeQuery(id+"F1.opExtrude","CAP_EDGE",EDGE,{"disambiguationData":[OSD([subQ0]),TDD([makeQuery(id+"F0.imprint","IMPRINT",EDGE,{"disambiguationData":[TD([[makeQuery(id+"F0.imprint","INTERSECT",VERTEX,{"disambiguationData":[OD(1.0)],"derivedFrom":[subQ0,sQuery(id+"F0.wireOp",EDGE,"E9.3.0")]}),1.0]])],"derivedFrom":subQ0})])],"isStart":true});}
            var Q53;
            {var subQ0=sQuery(id+"F0.wireOp",EDGE,"E2");Q53=makeQuery(id+"F1.opExtrude","CAP_EDGE",EDGE,{"disambiguationData":[OSD([subQ0]),TDD([makeQuery(id+"F0.imprint","IMPRINT",EDGE,{"disambiguationData":[TD([[makeQuery(id+"F0.imprint","INTERSECT",VERTEX,{"disambiguationData":[OD(1.0)],"derivedFrom":[subQ0,sQuery(id+"F0.wireOp",EDGE,"E9.2.0")]}),1.0]])],"derivedFrom":subQ0})])],"isStart":true});}
            var Q54;
            Q54=makeQuery(id+"F1.opExtrude","CAP_EDGE",EDGE,{"disambiguationData":[OSD([sQuery(id+"F0.wireOp",EDGE,"E3")])],"isStart":true});
            var Q55;
            {var subQ0=sQuery(id+"F0.wireOp",EDGE,"E1");Q55=makeQuery(id+"F1.opExtrude","CAP_EDGE",EDGE,{"disambiguationData":[OSD([subQ0]),TDD([makeQuery(id+"F0.imprint","IMPRINT",EDGE,{"disambiguationData":[TD([[makeQuery(id+"F0.imprint","INTERSECT",VERTEX,{"derivedFrom":[subQ0,sQuery(id+"F0.wireOp",EDGE,"E3")]}),-1.0]])],"derivedFrom":subQ0})])],"isStart":true});}
            var Q56;
            Q56=makeQuery(id+"F1.opExtrude","CAP_EDGE",EDGE,{"disambiguationData":[OSD([sQuery(id+"F0.wireOp",EDGE,"E6.1.7")])],"isStart":true});
            var Q57;
            Q57=makeQuery(id+"F1.opExtrude","CAP_EDGE",EDGE,{"disambiguationData":[OSD([sQuery(id+"F0.wireOp",EDGE,"E6.1.8")])],"isStart":true});
            var Q58;
            Q58=makeQuery(id+"F1.opExtrude","CAP_EDGE",EDGE,{"disambiguationData":[OSD([sQuery(id+"F0.wireOp",EDGE,"E6.2.7")])],"isStart":true});
            var Q59;
            Q59=makeQuery(id+"F1.opExtrude","CAP_EDGE",EDGE,{"disambiguationData":[OSD([sQuery(id+"F0.wireOp",EDGE,"E9.2.0")])],"isStart":false});
            var Q60;
            Q60=makeQuery(id+"F1.opExtrude","CAP_EDGE",EDGE,{"disambiguationData":[OSD([sQuery(id+"F0.wireOp",EDGE,"E9.1.0")])],"isStart":false});
            var Q61;
            Q61=makeQuery(id+"F1.opExtrude","CAP_EDGE",EDGE,{"disambiguationData":[OSD([sQuery(id+"F0.wireOp",EDGE,"E9.4.0")])],"isStart":false});
            var Q62;
            Q62=makeQuery(id+"F1.opExtrude","CAP_EDGE",EDGE,{"disambiguationData":[OSD([sQuery(id+"F0.wireOp",EDGE,"E9.5.0")])],"isStart":false});
            var Q63;
            Q63=makeQuery(id+"F1.opExtrude","CAP_EDGE",EDGE,{"disambiguationData":[OSD([sQuery(id+"F0.wireOp",EDGE,"E8")])],"isStart":false});
            var Q64;
            Q64=makeQuery(id+"F1.opExtrude","CAP_EDGE",EDGE,{"disambiguationData":[OSD([sQuery(id+"F0.wireOp",EDGE,"E10.2.0")])],"isStart":false});
            var Q65;
            Q65=makeQuery(id+"F1.opExtrude","CAP_EDGE",EDGE,{"disambiguationData":[OSD([sQuery(id+"F0.wireOp",EDGE,"E10.2.1")])],"isStart":false});
            var Q66;
            Q66=makeQuery(id+"F1.opExtrude","CAP_EDGE",EDGE,{"disambiguationData":[OSD([sQuery(id+"F0.wireOp",EDGE,"E10.2.2")])],"isStart":false});
            var Q67;
            Q67=makeQuery(id+"F1.opExtrude","CAP_EDGE",EDGE,{"disambiguationData":[OSD([sQuery(id+"F0.wireOp",EDGE,"E10.2.3")])],"isStart":false});
            var Q68;
            Q68=makeQuery(id+"F1.opExtrude","CAP_EDGE",EDGE,{"disambiguationData":[OSD([sQuery(id+"F0.wireOp",EDGE,"E10.2.4")])],"isStart":false});
            var Q69;
            Q69=makeQuery(id+"F1.opExtrude","CAP_EDGE",EDGE,{"disambiguationData":[OSD([sQuery(id+"F0.wireOp",EDGE,"E10.2.5")])],"isStart":false});
            var Q70;
            Q70=makeQuery(id+"F1.opExtrude","CAP_EDGE",EDGE,{"disambiguationData":[OSD([sQuery(id+"F0.wireOp",EDGE,"E10.1.1")])],"isStart":false});
            var Q71;
            Q71=makeQuery(id+"F1.opExtrude","CAP_EDGE",EDGE,{"disambiguationData":[OSD([sQuery(id+"F0.wireOp",EDGE,"E10.1.2")])],"isStart":false});
            var Q72;
            Q72=makeQuery(id+"F1.opExtrude","CAP_EDGE",EDGE,{"disambiguationData":[OSD([sQuery(id+"F0.wireOp",EDGE,"E10.1.3")])],"isStart":false});
            var Q73;
            Q73=makeQuery(id+"F1.opExtrude","CAP_EDGE",EDGE,{"disambiguationData":[OSD([sQuery(id+"F0.wireOp",EDGE,"E10.1.4")])],"isStart":false});
            var Q74;
            Q74=makeQuery(id+"F1.opExtrude","CAP_EDGE",EDGE,{"disambiguationData":[OSD([sQuery(id+"F0.wireOp",EDGE,"E10.1.5")])],"isStart":false});
            var Q75;
            Q75=makeQuery(id+"F1.opExtrude","CAP_EDGE",EDGE,{"disambiguationData":[OSD([sQuery(id+"F0.wireOp",EDGE,"E9.3.0")])],"isStart":false});
            var Q76;
            Q76=makeQuery(id+"F1.opExtrude","CAP_EDGE",EDGE,{"disambiguationData":[OSD([sQuery(id+"F0.wireOp",EDGE,"E10.1.0")])],"isStart":true});
            var Q77;
            Q77=makeQuery(id+"F1.opExtrude","CAP_EDGE",EDGE,{"disambiguationData":[OSD([sQuery(id+"F0.wireOp",EDGE,"E10.2.5")])],"isStart":true});
            var Q78;
            Q78=makeQuery(id+"F1.opExtrude","CAP_EDGE",EDGE,{"disambiguationData":[OSD([sQuery(id+"F0.wireOp",EDGE,"E10.2.4")])],"isStart":true});
            var Q79;
            Q79=makeQuery(id+"F1.opExtrude","CAP_EDGE",EDGE,{"disambiguationData":[OSD([sQuery(id+"F0.wireOp",EDGE,"E10.1.5")])],"isStart":true});
            var Q80;
            Q80=makeQuery(id+"F1.opExtrude","CAP_EDGE",EDGE,{"disambiguationData":[OSD([sQuery(id+"F0.wireOp",EDGE,"E10.1.4")])],"isStart":true});
            var Q81;
            Q81=makeQuery(id+"F1.opExtrude","CAP_EDGE",EDGE,{"disambiguationData":[OSD([sQuery(id+"F0.wireOp",EDGE,"E9.1.0")])],"isStart":true});
            var Q82;
            Q82=makeQuery(id+"F1.opExtrude","CAP_EDGE",EDGE,{"disambiguationData":[OSD([sQuery(id+"F0.wireOp",EDGE,"E8")])],"isStart":true});
            var Q83;
            Q83=makeQuery(id+"F1.opExtrude","CAP_EDGE",EDGE,{"disambiguationData":[OSD([sQuery(id+"F0.wireOp",EDGE,"E10.2.0")])],"isStart":true});
            var Q84;
            Q84=makeQuery(id+"F1.opExtrude","CAP_EDGE",EDGE,{"disambiguationData":[OSD([sQuery(id+"F0.wireOp",EDGE,"E10.2.1")])],"isStart":true});
            var Q85;
            Q85=makeQuery(id+"F1.opExtrude","CAP_EDGE",EDGE,{"disambiguationData":[OSD([sQuery(id+"F0.wireOp",EDGE,"E10.2.2")])],"isStart":true});
            var Q86;
            Q86=makeQuery(id+"F1.opExtrude","CAP_EDGE",EDGE,{"disambiguationData":[OSD([sQuery(id+"F0.wireOp",EDGE,"E10.2.3")])],"isStart":true});
            var Q87;
            Q87=makeQuery(id+"F1.opExtrude","CAP_EDGE",EDGE,{"disambiguationData":[OSD([sQuery(id+"F0.wireOp",EDGE,"E10.1.2")])],"isStart":true});
            var Q88;
            Q88=makeQuery(id+"F1.opExtrude","CAP_EDGE",EDGE,{"disambiguationData":[OSD([sQuery(id+"F0.wireOp",EDGE,"E10.1.3")])],"isStart":true});
            var Q89;
            Q89=makeQuery(id+"F1.opExtrude","CAP_EDGE",EDGE,{"disambiguationData":[OSD([sQuery(id+"F0.wireOp",EDGE,"E9.3.0")])],"isStart":true});
            var Q90;
            Q90=makeQuery(id+"F1.opExtrude","CAP_EDGE",EDGE,{"disambiguationData":[OSD([sQuery(id+"F0.wireOp",EDGE,"E9.4.0")])],"isStart":true});
            var Q91;
            Q91=makeQuery(id+"F1.opExtrude","CAP_EDGE",EDGE,{"disambiguationData":[OSD([sQuery(id+"F0.wireOp",EDGE,"E10.1.1")])],"isStart":true});
            var Q92;
            Q92=makeQuery(id+"F1.opExtrude","CAP_EDGE",EDGE,{"disambiguationData":[OSD([sQuery(id+"F0.wireOp",EDGE,"E9.5.0")])],"isStart":true});
            var Q93;
            Q93=makeQuery(id+"F1.opExtrude","CAP_EDGE",EDGE,{"disambiguationData":[OSD([sQuery(id+"F0.wireOp",EDGE,"E9.2.0")])],"isStart":true});
            var Q94;
            Q94=makeQuery(id+"F1.opExtrude","CAP_EDGE",EDGE,{"disambiguationData":[OSD([sQuery(id+"F0.wireOp",EDGE,"E10.1.0")])],"isStart":false});
            fillet(context, id + "F2", {"entities" : qUnion([Q0, Q1, Q2, Q3, Q4, Q5, Q6, Q7, Q8, Q9, Q10, Q11, Q12, Q13, Q14, Q15, Q16, Q17, Q18, Q19, Q20, Q21, Q22, Q23, Q24, Q25, Q26, Q27, Q28, Q29, Q30, Q31, Q32, Q33, Q34, Q35, Q36, Q37, Q38, Q39, Q40, Q41, Q42, Q43, Q44, Q45, Q46, Q47, Q48, Q49, Q50, Q51, Q52, Q53, Q54, Q55, Q56, Q57, Q58, Q59, Q60, Q61, Q62, Q63, Q64, Q65, Q66, Q67, Q68, Q69, Q70, Q71, Q72, Q73, Q74, Q75, Q76, Q77, Q78, Q79, Q80, Q81, Q82, Q83, Q84, Q85, Q86, Q87, Q88, Q89, Q90, Q91, Q92, Q93, Q94]), "radius" : 1 * mm, "tangentPropagation" : true, "allowEdgeOverflow" : false});
        }
        {
            var Q0;
            {var subQ0=sQuery(id+"F0.wireOp",EDGE,"E8");var subQ1=sQuery(id+"F0.wireOp",EDGE,"E2");Q0=makeQuery(id+"F1.opExtrude","SWEPT_EDGE",EDGE,{"disambiguationData":[OSD([subQ1,subQ0]),TDD([makeQuery(id+"F0.imprint","INTERSECT",VERTEX,{"disambiguationData":[OD(1.0)],"derivedFrom":[subQ1,subQ0]})])]});}
            var Q1;
            {var subQ0=sQuery(id+"F0.wireOp",EDGE,"E9.5.0");var subQ1=sQuery(id+"F0.wireOp",EDGE,"E2");Q1=makeQuery(id+"F1.opExtrude","SWEPT_EDGE",EDGE,{"disambiguationData":[OSD([subQ1,subQ0]),TDD([makeQuery(id+"F0.imprint","INTERSECT",VERTEX,{"disambiguationData":[OD(0.0)],"derivedFrom":[subQ1,subQ0]})])]});}
            var Q2;
            {var subQ0=sQuery(id+"F0.wireOp",EDGE,"E9.4.0");var subQ1=sQuery(id+"F0.wireOp",EDGE,"E2");Q2=makeQuery(id+"F1.opExtrude","SWEPT_EDGE",EDGE,{"disambiguationData":[OSD([subQ1,subQ0]),TDD([makeQuery(id+"F0.imprint","INTERSECT",VERTEX,{"disambiguationData":[OD(1.0)],"derivedFrom":[subQ1,subQ0]})])]});}
            var Q3;
            {var subQ0=sQuery(id+"F0.wireOp",EDGE,"E9.4.0");var subQ1=sQuery(id+"F0.wireOp",EDGE,"E2");Q3=makeQuery(id+"F1.opExtrude","SWEPT_EDGE",EDGE,{"disambiguationData":[OSD([subQ1,subQ0]),TDD([makeQuery(id+"F0.imprint","INTERSECT",VERTEX,{"disambiguationData":[OD(0.0)],"derivedFrom":[subQ1,subQ0]})])]});}
            var Q4;
            {var subQ0=sQuery(id+"F0.wireOp",EDGE,"E9.3.0");var subQ1=sQuery(id+"F0.wireOp",EDGE,"E2");Q4=makeQuery(id+"F1.opExtrude","SWEPT_EDGE",EDGE,{"disambiguationData":[OSD([subQ1,subQ0]),TDD([makeQuery(id+"F0.imprint","INTERSECT",VERTEX,{"disambiguationData":[OD(1.0)],"derivedFrom":[subQ1,subQ0]})])]});}
            var Q5;
            {var subQ0=sQuery(id+"F0.wireOp",EDGE,"E9.3.0");var subQ1=sQuery(id+"F0.wireOp",EDGE,"E2");Q5=makeQuery(id+"F1.opExtrude","SWEPT_EDGE",EDGE,{"disambiguationData":[OSD([subQ1,subQ0]),TDD([makeQuery(id+"F0.imprint","INTERSECT",VERTEX,{"disambiguationData":[OD(0.0)],"derivedFrom":[subQ1,subQ0]})])]});}
            var Q6;
            {var subQ0=sQuery(id+"F0.wireOp",EDGE,"E9.2.0");var subQ1=sQuery(id+"F0.wireOp",EDGE,"E2");Q6=makeQuery(id+"F1.opExtrude","SWEPT_EDGE",EDGE,{"disambiguationData":[OSD([subQ1,subQ0]),TDD([makeQuery(id+"F0.imprint","INTERSECT",VERTEX,{"disambiguationData":[OD(1.0)],"derivedFrom":[subQ1,subQ0]})])]});}
            var Q7;
            {var subQ0=sQuery(id+"F0.wireOp",EDGE,"E9.2.0");var subQ1=sQuery(id+"F0.wireOp",EDGE,"E2");Q7=makeQuery(id+"F1.opExtrude","SWEPT_EDGE",EDGE,{"disambiguationData":[OSD([subQ1,subQ0]),TDD([makeQuery(id+"F0.imprint","INTERSECT",VERTEX,{"disambiguationData":[OD(0.0)],"derivedFrom":[subQ1,subQ0]})])]});}
            var Q8;
            {var subQ0=sQuery(id+"F0.wireOp",EDGE,"E9.1.0");var subQ1=sQuery(id+"F0.wireOp",EDGE,"E2");Q8=makeQuery(id+"F1.opExtrude","SWEPT_EDGE",EDGE,{"disambiguationData":[OSD([subQ1,subQ0]),TDD([makeQuery(id+"F0.imprint","INTERSECT",VERTEX,{"disambiguationData":[OD(0.0)],"derivedFrom":[subQ1,subQ0]})])]});}
            var Q9;
            {var subQ0=sQuery(id+"F0.wireOp",EDGE,"E9.1.0");var subQ1=sQuery(id+"F0.wireOp",EDGE,"E2");Q9=makeQuery(id+"F1.opExtrude","SWEPT_EDGE",EDGE,{"disambiguationData":[OSD([subQ1,subQ0]),TDD([makeQuery(id+"F0.imprint","INTERSECT",VERTEX,{"disambiguationData":[OD(1.0)],"derivedFrom":[subQ1,subQ0]})])]});}
            var Q10;
            {var subQ0=sQuery(id+"F0.wireOp",EDGE,"E10.1.5");var subQ1=sQuery(id+"F0.wireOp",EDGE,"E6.1.0");Q10=makeQuery(id+"F1.opExtrude","SWEPT_EDGE",EDGE,{"disambiguationData":[OSD([subQ1,subQ0]),TDD([makeQuery(id+"F0.imprint","INTERSECT",VERTEX,{"disambiguationData":[OD(0.0)],"derivedFrom":[subQ1,subQ0]})])]});}
            var Q11;
            {var subQ0=sQuery(id+"F0.wireOp",EDGE,"E10.1.4");var subQ1=sQuery(id+"F0.wireOp",EDGE,"E6.1.0");Q11=makeQuery(id+"F1.opExtrude","SWEPT_EDGE",EDGE,{"disambiguationData":[OSD([subQ1,subQ0]),TDD([makeQuery(id+"F0.imprint","INTERSECT",VERTEX,{"disambiguationData":[OD(1.0)],"derivedFrom":[subQ1,subQ0]})])]});}
            var Q12;
            {var subQ0=sQuery(id+"F0.wireOp",EDGE,"E10.1.3");var subQ1=sQuery(id+"F0.wireOp",EDGE,"E6.1.0");Q12=makeQuery(id+"F1.opExtrude","SWEPT_EDGE",EDGE,{"disambiguationData":[OSD([subQ1,subQ0]),TDD([makeQuery(id+"F0.imprint","INTERSECT",VERTEX,{"disambiguationData":[OD(1.0)],"derivedFrom":[subQ1,subQ0]})])]});}
            var Q13;
            {var subQ0=sQuery(id+"F0.wireOp",EDGE,"E10.1.3");var subQ1=sQuery(id+"F0.wireOp",EDGE,"E6.1.0");Q13=makeQuery(id+"F1.opExtrude","SWEPT_EDGE",EDGE,{"disambiguationData":[OSD([subQ1,subQ0]),TDD([makeQuery(id+"F0.imprint","INTERSECT",VERTEX,{"disambiguationData":[OD(0.0)],"derivedFrom":[subQ1,subQ0]})])]});}
            var Q14;
            {var subQ0=sQuery(id+"F0.wireOp",EDGE,"E10.1.2");var subQ1=sQuery(id+"F0.wireOp",EDGE,"E6.1.0");Q14=makeQuery(id+"F1.opExtrude","SWEPT_EDGE",EDGE,{"disambiguationData":[OSD([subQ1,subQ0]),TDD([makeQuery(id+"F0.imprint","INTERSECT",VERTEX,{"disambiguationData":[OD(1.0)],"derivedFrom":[subQ1,subQ0]})])]});}
            var Q15;
            {var subQ0=sQuery(id+"F0.wireOp",EDGE,"E10.1.2");var subQ1=sQuery(id+"F0.wireOp",EDGE,"E6.1.0");Q15=makeQuery(id+"F1.opExtrude","SWEPT_EDGE",EDGE,{"disambiguationData":[OSD([subQ1,subQ0]),TDD([makeQuery(id+"F0.imprint","INTERSECT",VERTEX,{"disambiguationData":[OD(0.0)],"derivedFrom":[subQ1,subQ0]})])]});}
            var Q16;
            {var subQ0=sQuery(id+"F0.wireOp",EDGE,"E10.1.1");var subQ1=sQuery(id+"F0.wireOp",EDGE,"E6.1.0");Q16=makeQuery(id+"F1.opExtrude","SWEPT_EDGE",EDGE,{"disambiguationData":[OSD([subQ1,subQ0]),TDD([makeQuery(id+"F0.imprint","INTERSECT",VERTEX,{"disambiguationData":[OD(1.0)],"derivedFrom":[subQ1,subQ0]})])]});}
            var Q17;
            {var subQ0=sQuery(id+"F0.wireOp",EDGE,"E10.1.1");var subQ1=sQuery(id+"F0.wireOp",EDGE,"E6.1.0");Q17=makeQuery(id+"F1.opExtrude","SWEPT_EDGE",EDGE,{"disambiguationData":[OSD([subQ1,subQ0]),TDD([makeQuery(id+"F0.imprint","INTERSECT",VERTEX,{"disambiguationData":[OD(0.0)],"derivedFrom":[subQ1,subQ0]})])]});}
            var Q18;
            {var subQ0=sQuery(id+"F0.wireOp",EDGE,"E10.2.0");var subQ1=sQuery(id+"F0.wireOp",EDGE,"E6.2.0");Q18=makeQuery(id+"F1.opExtrude","SWEPT_EDGE",EDGE,{"disambiguationData":[OSD([subQ1,subQ0]),TDD([makeQuery(id+"F0.imprint","INTERSECT",VERTEX,{"disambiguationData":[OD(0.0)],"derivedFrom":[subQ1,subQ0]})])]});}
            var Q19;
            {var subQ0=sQuery(id+"F0.wireOp",EDGE,"E10.2.0");var subQ1=sQuery(id+"F0.wireOp",EDGE,"E6.2.0");Q19=makeQuery(id+"F1.opExtrude","SWEPT_EDGE",EDGE,{"disambiguationData":[OSD([subQ1,subQ0]),TDD([makeQuery(id+"F0.imprint","INTERSECT",VERTEX,{"disambiguationData":[OD(1.0)],"derivedFrom":[subQ1,subQ0]})])]});}
            var Q20;
            {var subQ0=sQuery(id+"F0.wireOp",EDGE,"E10.2.1");var subQ1=sQuery(id+"F0.wireOp",EDGE,"E6.2.0");Q20=makeQuery(id+"F1.opExtrude","SWEPT_EDGE",EDGE,{"disambiguationData":[OSD([subQ1,subQ0]),TDD([makeQuery(id+"F0.imprint","INTERSECT",VERTEX,{"disambiguationData":[OD(0.0)],"derivedFrom":[subQ1,subQ0]})])]});}
            var Q21;
            {var subQ0=sQuery(id+"F0.wireOp",EDGE,"E10.2.1");var subQ1=sQuery(id+"F0.wireOp",EDGE,"E6.2.0");Q21=makeQuery(id+"F1.opExtrude","SWEPT_EDGE",EDGE,{"disambiguationData":[OSD([subQ1,subQ0]),TDD([makeQuery(id+"F0.imprint","INTERSECT",VERTEX,{"disambiguationData":[OD(1.0)],"derivedFrom":[subQ1,subQ0]})])]});}
            var Q22;
            {var subQ0=sQuery(id+"F0.wireOp",EDGE,"E10.2.2");var subQ1=sQuery(id+"F0.wireOp",EDGE,"E6.2.0");Q22=makeQuery(id+"F1.opExtrude","SWEPT_EDGE",EDGE,{"disambiguationData":[OSD([subQ1,subQ0]),TDD([makeQuery(id+"F0.imprint","INTERSECT",VERTEX,{"disambiguationData":[OD(0.0)],"derivedFrom":[subQ1,subQ0]})])]});}
            var Q23;
            {var subQ0=sQuery(id+"F0.wireOp",EDGE,"E10.2.2");var subQ1=sQuery(id+"F0.wireOp",EDGE,"E6.2.0");Q23=makeQuery(id+"F1.opExtrude","SWEPT_EDGE",EDGE,{"disambiguationData":[OSD([subQ1,subQ0]),TDD([makeQuery(id+"F0.imprint","INTERSECT",VERTEX,{"disambiguationData":[OD(1.0)],"derivedFrom":[subQ1,subQ0]})])]});}
            var Q24;
            {var subQ0=sQuery(id+"F0.wireOp",EDGE,"E10.2.3");var subQ1=sQuery(id+"F0.wireOp",EDGE,"E6.2.0");Q24=makeQuery(id+"F1.opExtrude","SWEPT_EDGE",EDGE,{"disambiguationData":[OSD([subQ1,subQ0]),TDD([makeQuery(id+"F0.imprint","INTERSECT",VERTEX,{"disambiguationData":[OD(0.0)],"derivedFrom":[subQ1,subQ0]})])]});}
            var Q25;
            {var subQ0=sQuery(id+"F0.wireOp",EDGE,"E10.2.3");var subQ1=sQuery(id+"F0.wireOp",EDGE,"E6.2.0");Q25=makeQuery(id+"F1.opExtrude","SWEPT_EDGE",EDGE,{"disambiguationData":[OSD([subQ1,subQ0]),TDD([makeQuery(id+"F0.imprint","INTERSECT",VERTEX,{"disambiguationData":[OD(1.0)],"derivedFrom":[subQ1,subQ0]})])]});}
            var Q26;
            {var subQ0=sQuery(id+"F0.wireOp",EDGE,"E10.2.4");var subQ1=sQuery(id+"F0.wireOp",EDGE,"E6.2.0");Q26=makeQuery(id+"F1.opExtrude","SWEPT_EDGE",EDGE,{"disambiguationData":[OSD([subQ1,subQ0]),TDD([makeQuery(id+"F0.imprint","INTERSECT",VERTEX,{"disambiguationData":[OD(0.0)],"derivedFrom":[subQ1,subQ0]})])]});}
            var Q27;
            {var subQ0=sQuery(id+"F0.wireOp",EDGE,"E10.2.4");var subQ1=sQuery(id+"F0.wireOp",EDGE,"E6.2.0");Q27=makeQuery(id+"F1.opExtrude","SWEPT_EDGE",EDGE,{"disambiguationData":[OSD([subQ1,subQ0]),TDD([makeQuery(id+"F0.imprint","INTERSECT",VERTEX,{"disambiguationData":[OD(1.0)],"derivedFrom":[subQ1,subQ0]})])]});}
            var Q28;
            {var subQ0=sQuery(id+"F0.wireOp",EDGE,"E10.2.5");var subQ1=sQuery(id+"F0.wireOp",EDGE,"E6.2.0");Q28=makeQuery(id+"F1.opExtrude","SWEPT_EDGE",EDGE,{"disambiguationData":[OSD([subQ1,subQ0]),TDD([makeQuery(id+"F0.imprint","INTERSECT",VERTEX,{"disambiguationData":[OD(0.0)],"derivedFrom":[subQ1,subQ0]})])]});}
            var Q29;
            {var subQ0=sQuery(id+"F0.wireOp",EDGE,"E10.2.5");var subQ1=sQuery(id+"F0.wireOp",EDGE,"E6.2.0");Q29=makeQuery(id+"F1.opExtrude","SWEPT_EDGE",EDGE,{"disambiguationData":[OSD([subQ1,subQ0]),TDD([makeQuery(id+"F0.imprint","INTERSECT",VERTEX,{"disambiguationData":[OD(1.0)],"derivedFrom":[subQ1,subQ0]})])]});}
            var Q30;
            {var subQ0=sQuery(id+"F0.wireOp",EDGE,"E10.1.0");var subQ1=sQuery(id+"F0.wireOp",EDGE,"E6.1.0");Q30=makeQuery(id+"F1.opExtrude","SWEPT_EDGE",EDGE,{"disambiguationData":[OSD([subQ1,subQ0]),TDD([makeQuery(id+"F0.imprint","INTERSECT",VERTEX,{"disambiguationData":[OD(1.0)],"derivedFrom":[subQ1,subQ0]})])]});}
            var Q31;
            {var subQ0=sQuery(id+"F0.wireOp",EDGE,"E10.1.0");var subQ1=sQuery(id+"F0.wireOp",EDGE,"E6.1.0");Q31=makeQuery(id+"F1.opExtrude","SWEPT_EDGE",EDGE,{"disambiguationData":[OSD([subQ1,subQ0]),TDD([makeQuery(id+"F0.imprint","INTERSECT",VERTEX,{"disambiguationData":[OD(0.0)],"derivedFrom":[subQ1,subQ0]})])]});}
            var Q32;
            {var subQ0=sQuery(id+"F0.wireOp",EDGE,"E10.1.5");var subQ1=sQuery(id+"F0.wireOp",EDGE,"E6.1.0");Q32=makeQuery(id+"F1.opExtrude","SWEPT_EDGE",EDGE,{"disambiguationData":[OSD([subQ1,subQ0]),TDD([makeQuery(id+"F0.imprint","INTERSECT",VERTEX,{"disambiguationData":[OD(1.0)],"derivedFrom":[subQ1,subQ0]})])]});}
            var Q33;
            {var subQ0=sQuery(id+"F0.wireOp",EDGE,"E10.1.4");var subQ1=sQuery(id+"F0.wireOp",EDGE,"E6.1.0");Q33=makeQuery(id+"F1.opExtrude","SWEPT_EDGE",EDGE,{"disambiguationData":[OSD([subQ1,subQ0]),TDD([makeQuery(id+"F0.imprint","INTERSECT",VERTEX,{"disambiguationData":[OD(0.0)],"derivedFrom":[subQ1,subQ0]})])]});}
            var Q34;
            {var subQ0=sQuery(id+"F0.wireOp",EDGE,"E9.5.0");var subQ1=sQuery(id+"F0.wireOp",EDGE,"E2");Q34=makeQuery(id+"F1.opExtrude","SWEPT_EDGE",EDGE,{"disambiguationData":[OSD([subQ1,subQ0]),TDD([makeQuery(id+"F0.imprint","INTERSECT",VERTEX,{"disambiguationData":[OD(1.0)],"derivedFrom":[subQ1,subQ0]})])]});}
            var Q35;
            {var subQ0=sQuery(id+"F0.wireOp",EDGE,"E8");var subQ1=sQuery(id+"F0.wireOp",EDGE,"E2");Q35=makeQuery(id+"F1.opExtrude","SWEPT_EDGE",EDGE,{"disambiguationData":[OSD([subQ1,subQ0]),TDD([makeQuery(id+"F0.imprint","INTERSECT",VERTEX,{"disambiguationData":[OD(0.0)],"derivedFrom":[subQ1,subQ0]})])]});}
            var Q36;
            Q36=makeQuery(id+"F1.opExtrude","SWEPT_EDGE",EDGE,{"disambiguationData":[OSD([sQuery(id+"F0.wireOp",EDGE,"E1"),sQuery(id+"F0.wireOp",EDGE,"E6.1.8")])]});
            var Q37;
            Q37=makeQuery(id+"F1.opExtrude","SWEPT_EDGE",EDGE,{"disambiguationData":[OSD([sQuery(id+"F0.wireOp",EDGE,"E1"),sQuery(id+"F0.wireOp",EDGE,"E6.2.7")])]});
            var Q38;
            Q38=makeQuery(id+"F1.opExtrude","SWEPT_EDGE",EDGE,{"disambiguationData":[OSD([sQuery(id+"F0.wireOp",EDGE,"E6.1.0"),sQuery(id+"F0.wireOp",EDGE,"E6.1.8")])]});
            var Q39;
            Q39=makeQuery(id+"F1.opExtrude","SWEPT_EDGE",EDGE,{"disambiguationData":[OSD([sQuery(id+"F0.wireOp",EDGE,"E6.1.0"),sQuery(id+"F0.wireOp",EDGE,"E6.1.7")])]});
            var Q40;
            Q40=makeQuery(id+"F1.opExtrude","SWEPT_EDGE",EDGE,{"disambiguationData":[OSD([sQuery(id+"F0.wireOp",EDGE,"E1"),sQuery(id+"F0.wireOp",EDGE,"E6.1.7")])]});
            var Q41;
            Q41=makeQuery(id+"F1.opExtrude","SWEPT_EDGE",EDGE,{"disambiguationData":[OSD([sQuery(id+"F0.wireOp",EDGE,"E1"),sQuery(id+"F0.wireOp",EDGE,"E3")])]});
            var Q42;
            Q42=makeQuery(id+"F1.opExtrude","SWEPT_EDGE",EDGE,{"disambiguationData":[OSD([sQuery(id+"F0.wireOp",EDGE,"E1"),sQuery(id+"F0.wireOp",EDGE,"E4")])]});
            var Q43;
            Q43=makeQuery(id+"F1.opExtrude","SWEPT_EDGE",EDGE,{"disambiguationData":[OSD([sQuery(id+"F0.wireOp",EDGE,"E1"),sQuery(id+"F0.wireOp",EDGE,"E6.2.8")])]});
            var Q44;
            Q44=makeQuery(id+"F1.opExtrude","SWEPT_EDGE",EDGE,{"disambiguationData":[OSD([sQuery(id+"F0.wireOp",EDGE,"E6.2.0"),sQuery(id+"F0.wireOp",EDGE,"E6.2.8")])]});
            var Q45;
            Q45=makeQuery(id+"F1.opExtrude","SWEPT_EDGE",EDGE,{"disambiguationData":[OSD([sQuery(id+"F0.wireOp",EDGE,"E2"),sQuery(id+"F0.wireOp",EDGE,"E3")])]});
            var Q46;
            Q46=makeQuery(id+"F1.opExtrude","SWEPT_EDGE",EDGE,{"disambiguationData":[OSD([sQuery(id+"F0.wireOp",EDGE,"E2"),sQuery(id+"F0.wireOp",EDGE,"E4")])]});
            var Q47;
            Q47=makeQuery(id+"F1.opExtrude","SWEPT_EDGE",EDGE,{"disambiguationData":[OSD([sQuery(id+"F0.wireOp",EDGE,"E6.2.0"),sQuery(id+"F0.wireOp",EDGE,"E6.2.7")])]});
            fillet(context, id + "F3", {"entities" : qUnion([Q0, Q1, Q2, Q3, Q4, Q5, Q6, Q7, Q8, Q9, Q10, Q11, Q12, Q13, Q14, Q15, Q16, Q17, Q18, Q19, Q20, Q21, Q22, Q23, Q24, Q25, Q26, Q27, Q28, Q29, Q30, Q31, Q32, Q33, Q34, Q35, Q36, Q37, Q38, Q39, Q40, Q41, Q42, Q43, Q44, Q45, Q46, Q47]), "radius" : 1 * mm, "tangentPropagation" : true, "allowEdgeOverflow" : false});
        }
        {
            var Q0;
            Q0=makeQuery(id+"F1.opExtrude","CAP_FACE",FACE,{"disambiguationData":[OSD([sQuery(id+"F0.wireOp",EDGE,"E0"),sQuery(id+"F0.wireOp",EDGE,"E1"),sQuery(id+"F0.wireOp",EDGE,"E2"),sQuery(id+"F0.wireOp",EDGE,"E3"),sQuery(id+"F0.wireOp",EDGE,"E4"),sQuery(id+"F0.wireOp",EDGE,"E5.0"),sQuery(id+"F0.wireOp",EDGE,"E5.1"),sQuery(id+"F0.wireOp",EDGE,"E5.2"),sQuery(id+"F0.wireOp",EDGE,"E5.3"),sQuery(id+"F0.wireOp",EDGE,"E5.4"),sQuery(id+"F0.wireOp",EDGE,"E5.5"),sQuery(id+"F0.wireOp",EDGE,"E6.1.0"),sQuery(id+"F0.wireOp",EDGE,"E6.1.1"),sQuery(id+"F0.wireOp",EDGE,"E6.1.2"),sQuery(id+"F0.wireOp",EDGE,"E6.1.3"),sQuery(id+"F0.wireOp",EDGE,"E6.1.4"),sQuery(id+"F0.wireOp",EDGE,"E6.1.5"),sQuery(id+"F0.wireOp",EDGE,"E6.1.6"),sQuery(id+"F0.wireOp",EDGE,"E6.1.7"),sQuery(id+"F0.wireOp",EDGE,"E6.1.8"),sQuery(id+"F0.wireOp",EDGE,"E6.2.0"),sQuery(id+"F0.wireOp",EDGE,"E6.2.1"),sQuery(id+"F0.wireOp",EDGE,"E6.2.2"),sQuery(id+"F0.wireOp",EDGE,"E6.2.3"),sQuery(id+"F0.wireOp",EDGE,"E6.2.4"),sQuery(id+"F0.wireOp",EDGE,"E6.2.5"),sQuery(id+"F0.wireOp",EDGE,"E6.2.6"),sQuery(id+"F0.wireOp",EDGE,"E6.2.7"),sQuery(id+"F0.wireOp",EDGE,"E6.2.8"),sQuery(id+"F0.wireOp",EDGE,"E8"),sQuery(id+"F0.wireOp",EDGE,"E9.1.0"),sQuery(id+"F0.wireOp",EDGE,"E9.2.0"),sQuery(id+"F0.wireOp",EDGE,"E9.3.0"),sQuery(id+"F0.wireOp",EDGE,"E9.4.0"),sQuery(id+"F0.wireOp",EDGE,"E9.5.0"),sQuery(id+"F0.wireOp",EDGE,"E10.1.0"),sQuery(id+"F0.wireOp",EDGE,"E10.1.1"),sQuery(id+"F0.wireOp",EDGE,"E10.1.2"),sQuery(id+"F0.wireOp",EDGE,"E10.1.3"),sQuery(id+"F0.wireOp",EDGE,"E10.1.4"),sQuery(id+"F0.wireOp",EDGE,"E10.1.5"),sQuery(id+"F0.wireOp",EDGE,"E10.2.0"),sQuery(id+"F0.wireOp",EDGE,"E10.2.1"),sQuery(id+"F0.wireOp",EDGE,"E10.2.2"),sQuery(id+"F0.wireOp",EDGE,"E10.2.3"),sQuery(id+"F0.wireOp",EDGE,"E10.2.4"),sQuery(id+"F0.wireOp",EDGE,"E10.2.5")])],"isStart":false});
            var sketch = newSketch(context, id + "F4", { "sketchPlane" : qUnion([Q0])});
            skText(sketch, "E11", { "text": "T", "fontName": "OpenSans-Bold.ttf"});
            skText(sketch, "E12", { "text": "m", "fontName": "OpenSans-Bold.ttf"});
            skLineSegment(sketch, "E13", {"start": v(0, 0.03) * mm, "end": v(-9.35, 16.23) * mm, "construction": true});
            skText(sketch, "E14", { "text": "o", "fontName": "OpenSans-Bold.ttf"});
            skLineSegment(sketch, "E15", {"start": v(0, 0.03) * mm, "end": v(-9.13, -16.29) * mm, "construction": true});
            const initialGuessF4  = {"E11": [0.007, 0.00352, 0, -1, 0.00808], "E12": [-0.00808, 0.00703, 0.86603, 0.5, 0.00519], "E14": [-0.01025, -0.01112, 0.87263, -0.48839, 0.00789]};
            skSetInitialGuess(sketch, initialGuessF4);
            skSolve(sketch);
        }
        {
            var Q0;
            Q0 = qSketchRegion(id + "F4", true);
            extrude(context, id + "F5", {"entities" : qUnion([Q0]), "operationType" : NewBodyOperationType.REMOVE, "oppositeDirection" : true, "depth" : 2 * mm, "offsetDistance" : 25 * mm});
        }
    });
